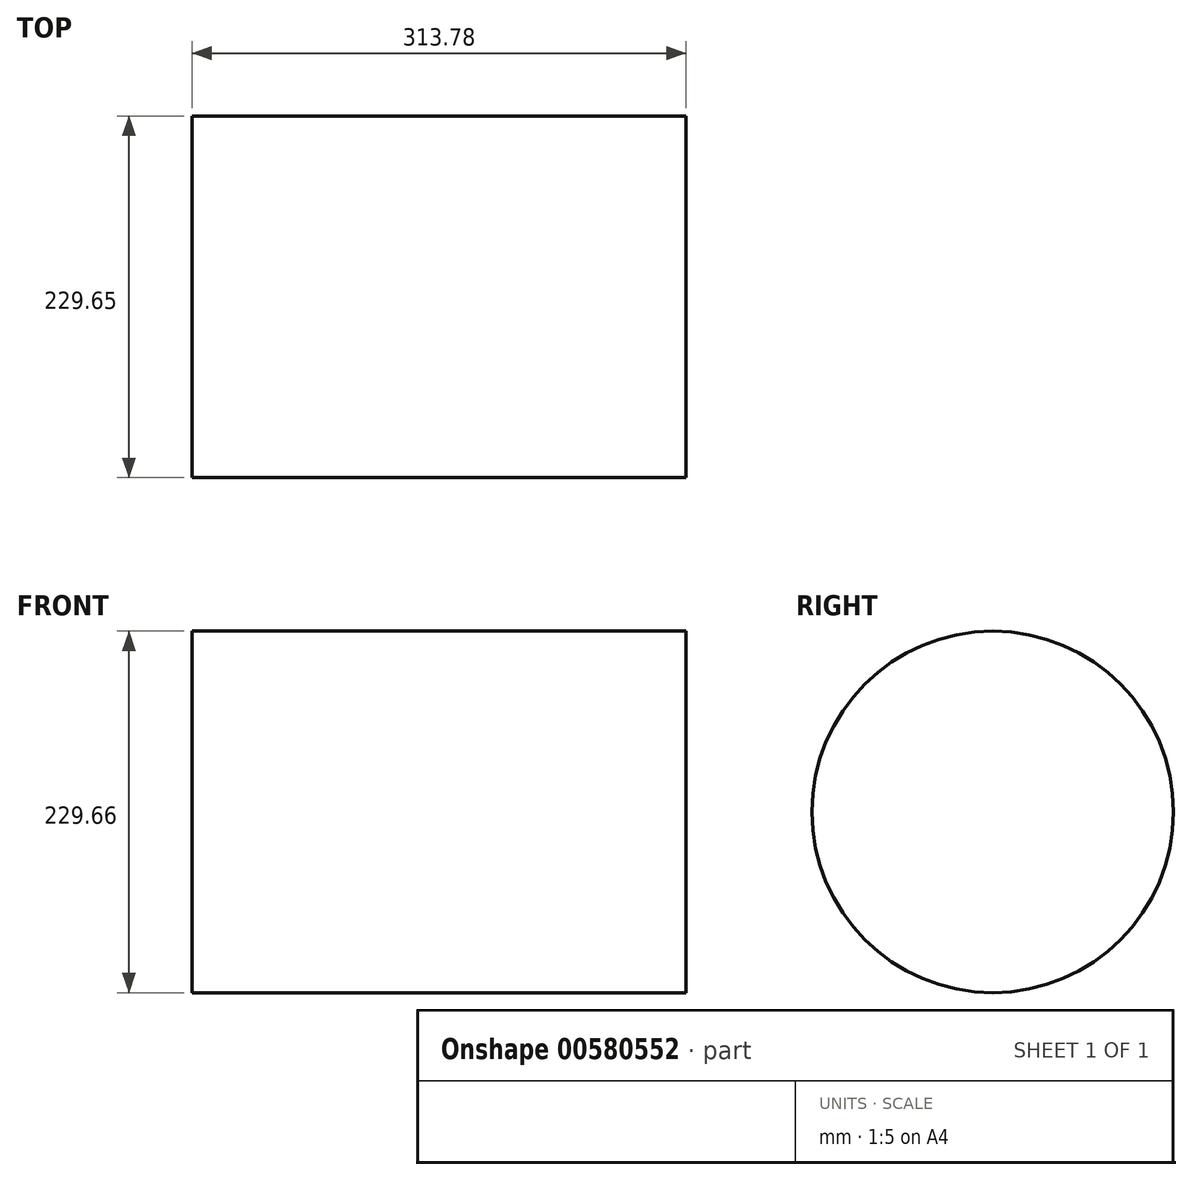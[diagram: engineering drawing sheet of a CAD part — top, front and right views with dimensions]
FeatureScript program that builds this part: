
annotation { "Feature Type Name" : "Feature", "Feature Type Description" : "" }
export const myFeature = defineFeature(function(context is Context, id is Id, definition is map)
    precondition{}
    {
        {
            var Q0;
            Q0=qCreatedBy(makeId("Top.planeOp"),FACE);
            var sketch = newSketch(context, id + "F0", { "sketchPlane" : qUnion([Q0])});
            skLineSegment(sketch, "E0.bottom", {"start": v(-186.26, 67.74) * mm, "end": v(127.52, 67.74) * mm});
            skLineSegment(sketch, "E0.top", {"start": v(-186.26, -47.09) * mm, "end": v(127.52, -47.09) * mm});
            skLineSegment(sketch, "E0.left", {"start": v(-186.26, 67.74) * mm, "end": v(-186.26, -47.09) * mm});
            skLineSegment(sketch, "E0.right", {"start": v(127.52, 67.74) * mm, "end": v(127.52, -47.09) * mm});
            skSolve(sketch);
        }
        {
            var Q0;
            Q0=makeQuery(id+"F0.imprint","IMPRINT",FACE,{"disambiguationData":[TD([[makeQuery(id+"F0.imprint","IMPRINT",EDGE,{"derivedFrom":sQuery(id+"F0.wireOp",EDGE,"E0.bottom")}),-1.0]])]});
            var Q1;
            Q1=sQuery(id+"F0.wireOp",EDGE,"E0.bottom");
            revolve(context, id + "F1", {"entities" : qUnion([Q0]), "axis" : qUnion([Q1]), "revolveType" : RevolveType.FULL});
        }
    });
